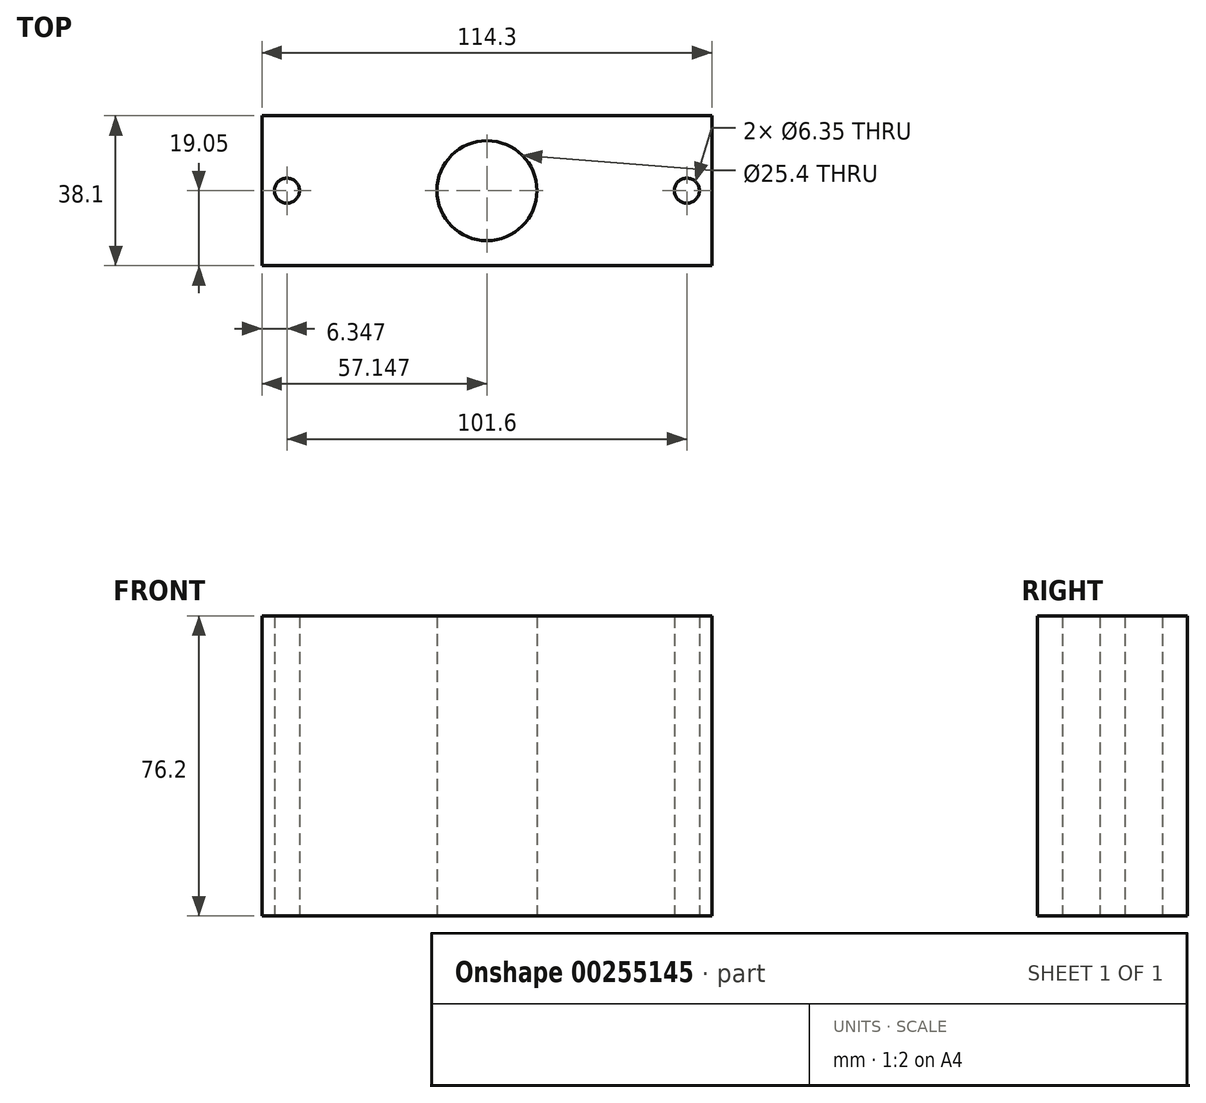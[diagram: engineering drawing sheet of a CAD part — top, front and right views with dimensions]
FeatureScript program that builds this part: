
annotation { "Feature Type Name" : "Feature", "Feature Type Description" : "" }
export const myFeature = defineFeature(function(context is Context, id is Id, definition is map)
    precondition{}
    {
        {
            var Q0;
            Q0=qCreatedBy(makeId("Top.planeOp"),FACE);
            var sketch = newSketch(context, id + "F0", { "sketchPlane" : qUnion([Q0])});
            skLineSegment(sketch, "E0.bottom", {"start": v(-27.27, 0) * mm, "end": v(87.03, 0) * mm});
            skLineSegment(sketch, "E0.top", {"start": v(-27.27, 38.1) * mm, "end": v(87.03, 38.1) * mm});
            skLineSegment(sketch, "E0.left", {"start": v(-27.27, 0) * mm, "end": v(-27.27, 38.1) * mm});
            skLineSegment(sketch, "E0.right", {"start": v(87.03, 0) * mm, "end": v(87.03, 38.1) * mm});
            skSolve(sketch);
        }
        {
            var Q0;
            Q0 = qSketchRegion(id + "F0", true);
            extrude(context, id + "F1", {"entities" : qUnion([Q0]), "depth" : 76.2 * mm});
        }
        {
            var Q0;
            Q0=qCreatedBy(makeId("Top.planeOp"),FACE);
            var sketch = newSketch(context, id + "F2", { "sketchPlane" : qUnion([Q0])});
            skCircle(sketch, "E1", {"center": v(29.88, 19.05) * mm, "radius": 12.7 * mm});
            skSolve(sketch);
        }
        {
            var Q0;
            Q0 = qSketchRegion(id + "F2", true);
            extrude(context, id + "F3", {"entities" : qUnion([Q0]), "operationType" : NewBodyOperationType.REMOVE, "depth" : 85.6 * mm});
        }
        {
            var Q0;
            Q0=qCreatedBy(makeId("Top.planeOp"),FACE);
            var sketch = newSketch(context, id + "F4", { "sketchPlane" : qUnion([Q0])});
            skCircle(sketch, "E2", {"center": v(-20.92, 19.05) * mm, "radius": 3.17 * mm});
            skSolve(sketch);
        }
        {
            var Q0;
            Q0 = qSketchRegion(id + "F4", true);
            extrude(context, id + "F5", {"entities" : qUnion([Q0]), "operationType" : NewBodyOperationType.REMOVE, "depth" : 90.68 * mm});
        }
        {
            var Q0;
            Q0=qCreatedBy(makeId("Top.planeOp"),FACE);
            var sketch = newSketch(context, id + "F6", { "sketchPlane" : qUnion([Q0])});
            skCircle(sketch, "E3", {"center": v(80.68, 19.05) * mm, "radius": 3.17 * mm});
            skSolve(sketch);
        }
        {
            var Q0;
            Q0 = qSketchRegion(id + "F6", true);
            extrude(context, id + "F7", {"entities" : qUnion([Q0]), "operationType" : NewBodyOperationType.REMOVE, "depth" : 90.68 * mm});
        }
    });
